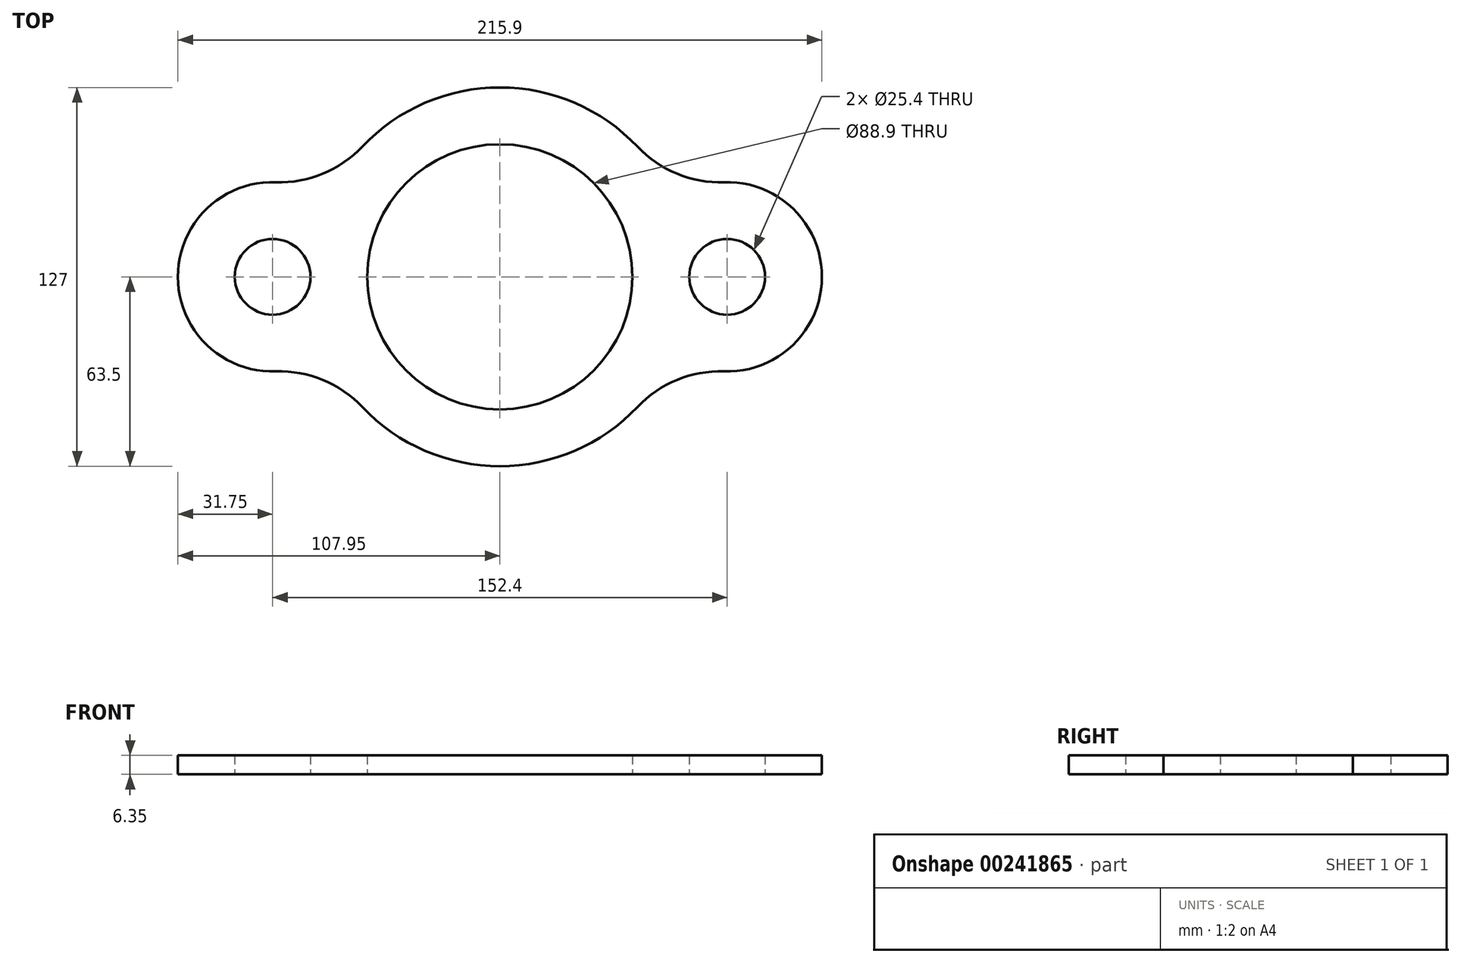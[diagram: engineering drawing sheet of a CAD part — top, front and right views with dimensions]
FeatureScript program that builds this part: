
annotation { "Feature Type Name" : "Feature", "Feature Type Description" : "" }
export const myFeature = defineFeature(function(context is Context, id is Id, definition is map)
    precondition{}
    {
        {
            var Q0;
            Q0=qCreatedBy(makeId("Top.planeOp"),FACE);
            var sketch = newSketch(context, id + "F0", { "sketchPlane" : qUnion([Q0])});
            skArc(sketch, "E0", {"start": v(-46.14, -43.63) * mm, "mid": v(0, -63.5) * mm, "end": v(46.14, -43.63) * mm});
            skCircle(sketch, "E1", {"center": v(0, 0) * mm, "radius": 44.45 * mm});
            skArc(sketch, "E2", {"start": v(75.12, -31.73) * mm, "mid": v(107.95, 0) * mm, "end": v(75.12, 31.73) * mm});
            skCircle(sketch, "E3", {"center": v(76.2, 0) * mm, "radius": 12.7 * mm});
            skArc(sketch, "E4", {"start": v(-75.12, 31.73) * mm, "mid": v(-107.95, 0) * mm, "end": v(-75.12, -31.73) * mm});
            skCircle(sketch, "E5", {"center": v(-76.2, 0) * mm, "radius": 12.7 * mm});
            skArc(sketch, "E6.trimOffspring", {"start": v(46.14, 43.63) * mm, "mid": v(0, 63.5) * mm, "end": v(-46.14, 43.63) * mm});
            skPoint(sketch, "E7.visualSharp", {"position": v(-57.94, 25.98) * mm});
            skArc(sketch, "E7.filletArc", {"start": v(-75.12, 31.73) * mm, "mid": v(-59.35, 34.56) * mm, "end": v(-46.14, 43.63) * mm});
            skPoint(sketch, "E8.visualSharp", {"position": v(57.94, 25.98) * mm});
            skArc(sketch, "E8.filletArc", {"start": v(46.14, 43.63) * mm, "mid": v(59.35, 34.56) * mm, "end": v(75.12, 31.73) * mm});
            skPoint(sketch, "E9.visualSharp", {"position": v(57.94, -25.98) * mm});
            skArc(sketch, "E9.filletArc", {"start": v(75.12, -31.73) * mm, "mid": v(59.35, -34.56) * mm, "end": v(46.14, -43.63) * mm});
            skPoint(sketch, "E10.visualSharp", {"position": v(-57.94, -25.98) * mm});
            skArc(sketch, "E10.filletArc", {"start": v(-46.14, -43.63) * mm, "mid": v(-59.35, -34.56) * mm, "end": v(-75.12, -31.73) * mm});
            skSolve(sketch);
        }
        {
            var Q0;
            Q0=makeQuery(id+"F0.imprint","IMPRINT",FACE,{"disambiguationData":[TD([[makeQuery(id+"F0.imprint","IMPRINT",EDGE,{"derivedFrom":sQuery(id+"F0.wireOp",EDGE,"E0")}),1.0]])]});
            extrude(context, id + "F1", {"entities" : qUnion([Q0]), "depth" : 6.35 * mm});
        }
    });
